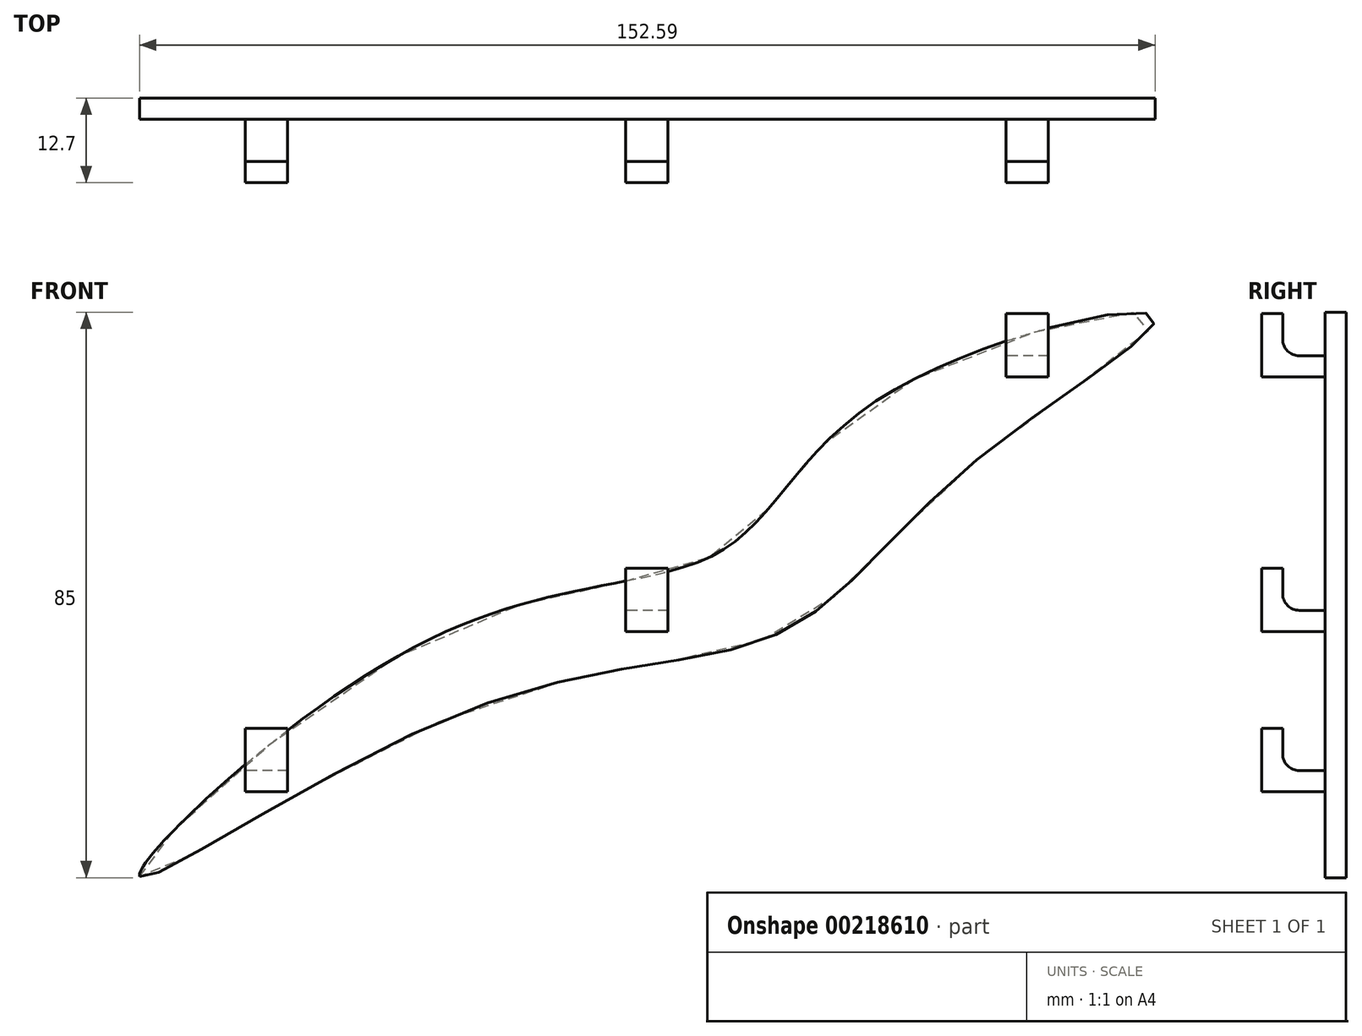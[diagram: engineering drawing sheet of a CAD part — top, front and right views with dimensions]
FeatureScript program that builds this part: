
annotation { "Feature Type Name" : "Feature", "Feature Type Description" : "" }
export const myFeature = defineFeature(function(context is Context, id is Id, definition is map)
    precondition{}
    {
        {
            var Q0;
            Q0=qCreatedBy(makeId("Front.planeOp"),FACE);
            var sketch = newSketch(context, id + "F0", { "sketchPlane" : qUnion([Q0])});
            skFitSpline(sketch, "E0", {"points": [v(0, 0) * mm, v(43.31, 35.58) * mm, v(87.55, 49.08) * mm, v(110.94, 71.7) * mm, v(152.4, 84.17) * mm, v(125.2, 62.2) * mm, v(96.47, 36.79) * mm, v(49.64, 25.18) * mm, v(0, 0) * mm]});
            skSolve(sketch);
        }
        {
            var Q0;
            Q0 = qSketchRegion(id + "F0", true);
            extrude(context, id + "F1", {"entities" : qUnion([Q0]), "depth" : 3.17 * mm});
        }
        {
            var Q0;
            Q0=qCreatedBy(makeId("Right.planeOp"),FACE);
            cPlane(context, id + "F2", {"entities" : qUnion([Q0]), "cplaneType" : CPlaneType.OFFSET, "offset" : 19.05 * mm, "width" : 152.4 * mm, "height" : 152.4 * mm});
        }
        {
            var Q0;
            Q0=qCreatedBy(id+"F2.planeOp",FACE);
            var sketch = newSketch(context, id + "F3", { "sketchPlane" : qUnion([Q0])});
            skLineSegment(sketch, "E1", {"start": v(-3.17, 12.76) * mm, "end": v(-12.7, 12.76) * mm});
            skLineSegment(sketch, "E2", {"start": v(-12.7, 12.76) * mm, "end": v(-12.7, 22.28) * mm});
            skLineSegment(sketch, "E3", {"start": v(-12.7, 22.28) * mm, "end": v(-9.52, 22.28) * mm});
            skLineSegment(sketch, "E4", {"start": v(-9.52, 22.28) * mm, "end": v(-9.52, 15.93) * mm});
            skLineSegment(sketch, "E5", {"start": v(-9.52, 15.93) * mm, "end": v(-3.18, 15.93) * mm});
            skLineSegment(sketch, "E6", {"start": v(-3.18, 15.93) * mm, "end": v(-3.18, 12.76) * mm});
            skSolve(sketch);
        }
        {
            var Q0;
            Q0 = qSketchRegion(id + "F3", true);
            extrude(context, id + "F4", {"entities" : qUnion([Q0]), "operationType" : NewBodyOperationType.ADD, "depth" : 6.35 * mm, "symmetric" : true});
        }
        {
            var Q0;
            Q0=qCreatedBy(makeId("Right.planeOp"),FACE);
            cPlane(context, id + "F5", {"entities" : qUnion([Q0]), "cplaneType" : CPlaneType.OFFSET, "offset" : 76.2 * mm, "width" : 152.4 * mm, "height" : 152.4 * mm});
        }
        {
            var Q0;
            Q0=qCreatedBy(id+"F5.planeOp",FACE);
            var sketch = newSketch(context, id + "F6", { "sketchPlane" : qUnion([Q0])});
            skLineSegment(sketch, "E7", {"start": v(-3.18, 36.86) * mm, "end": v(-12.7, 36.86) * mm});
            skLineSegment(sketch, "E8", {"start": v(-12.7, 36.86) * mm, "end": v(-12.7, 46.38) * mm});
            skLineSegment(sketch, "E9", {"start": v(-12.7, 46.38) * mm, "end": v(-9.53, 46.38) * mm});
            skLineSegment(sketch, "E10", {"start": v(-9.53, 46.38) * mm, "end": v(-9.53, 40.03) * mm});
            skLineSegment(sketch, "E11", {"start": v(-9.53, 40.03) * mm, "end": v(-3.18, 40.03) * mm});
            skLineSegment(sketch, "E12", {"start": v(-3.18, 40.03) * mm, "end": v(-3.18, 36.86) * mm});
            skSolve(sketch);
        }
        {
            var Q0;
            Q0 = qSketchRegion(id + "F6", true);
            extrude(context, id + "F7", {"entities" : qUnion([Q0]), "operationType" : NewBodyOperationType.ADD, "depth" : 6.35 * mm, "symmetric" : true});
        }
        {
            var Q0;
            Q0=qCreatedBy(makeId("Right.planeOp"),FACE);
            cPlane(context, id + "F8", {"entities" : qUnion([Q0]), "cplaneType" : CPlaneType.OFFSET, "offset" : 133.35 * mm, "width" : 152.4 * mm, "height" : 152.4 * mm});
        }
        {
            var Q0;
            Q0=qCreatedBy(id+"F8.planeOp",FACE);
            var sketch = newSketch(context, id + "F9", { "sketchPlane" : qUnion([Q0])});
            skLineSegment(sketch, "E13", {"start": v(-3.18, 75.11) * mm, "end": v(-12.7, 75.11) * mm});
            skLineSegment(sketch, "E14", {"start": v(-12.7, 75.11) * mm, "end": v(-12.7, 84.64) * mm});
            skLineSegment(sketch, "E15", {"start": v(-12.7, 84.64) * mm, "end": v(-9.53, 84.64) * mm});
            skLineSegment(sketch, "E16", {"start": v(-9.53, 84.64) * mm, "end": v(-9.53, 78.29) * mm});
            skLineSegment(sketch, "E17", {"start": v(-9.53, 78.29) * mm, "end": v(-3.17, 78.29) * mm});
            skLineSegment(sketch, "E18", {"start": v(-3.17, 78.29) * mm, "end": v(-3.17, 75.11) * mm});
            skSolve(sketch);
        }
        {
            var Q0;
            Q0 = qSketchRegion(id + "F9", true);
            extrude(context, id + "F10", {"entities" : qUnion([Q0]), "operationType" : NewBodyOperationType.ADD, "depth" : 6.35 * mm, "symmetric" : true});
        }
        {
            var Q0;
            Q0=makeQuery(id+"F4.opExtrude","SWEPT_EDGE",EDGE,{"disambiguationData":[OSD([sQuery(id+"F3.wireOp",EDGE,"E1"),sQuery(id+"F3.wireOp",EDGE,"E6")])]});
            var Q1;
            Q1=makeQuery(id+"F4.opExtrude","CAP_EDGE",EDGE,{"disambiguationData":[OSD([sQuery(id+"F3.wireOp",EDGE,"E6")])],"isStart":false});
            var Q2;
            Q2=makeQuery(id+"F4.opExtrude","CAP_EDGE",EDGE,{"disambiguationData":[OSD([sQuery(id+"F3.wireOp",EDGE,"E6")])],"isStart":true});
            var Q3;
            Q3=makeQuery(id+"F4.opExtrude","SWEPT_EDGE",EDGE,{"disambiguationData":[OSD([sQuery(id+"F3.wireOp",EDGE,"E5"),sQuery(id+"F3.wireOp",EDGE,"E6")])]});
            var Q4;
            Q4=makeQuery(id+"F4.opExtrude","SWEPT_EDGE",EDGE,{"disambiguationData":[OSD([sQuery(id+"F3.wireOp",EDGE,"E4"),sQuery(id+"F3.wireOp",EDGE,"E5")])]});
            var Q5;
            Q5=makeQuery(id+"F7.opExtrude","SWEPT_EDGE",EDGE,{"disambiguationData":[OSD([sQuery(id+"F6.wireOp",EDGE,"E11"),sQuery(id+"F6.wireOp",EDGE,"E12")])]});
            var Q6;
            Q6=makeQuery(id+"F7.opExtrude","CAP_EDGE",EDGE,{"disambiguationData":[OSD([sQuery(id+"F6.wireOp",EDGE,"E12")])],"isStart":true});
            var Q7;
            Q7=makeQuery(id+"F7.opExtrude","SWEPT_EDGE",EDGE,{"disambiguationData":[OSD([sQuery(id+"F6.wireOp",EDGE,"E7"),sQuery(id+"F6.wireOp",EDGE,"E12")])]});
            var Q8;
            Q8=makeQuery(id+"F7.opExtrude","CAP_EDGE",EDGE,{"disambiguationData":[OSD([sQuery(id+"F6.wireOp",EDGE,"E12")])],"isStart":false});
            var Q9;
            Q9=makeQuery(id+"F7.opExtrude","SWEPT_EDGE",EDGE,{"disambiguationData":[OSD([sQuery(id+"F6.wireOp",EDGE,"E10"),sQuery(id+"F6.wireOp",EDGE,"E11")])]});
            var Q10;
            Q10=makeQuery(id+"F10.opExtrude","CAP_EDGE",EDGE,{"disambiguationData":[OSD([sQuery(id+"F9.wireOp",EDGE,"E18")])],"isStart":false});
            var Q11;
            Q11=makeQuery(id+"F10.opExtrude","SWEPT_EDGE",EDGE,{"disambiguationData":[OSD([sQuery(id+"F9.wireOp",EDGE,"E17"),sQuery(id+"F9.wireOp",EDGE,"E18")])]});
            var Q12;
            Q12=makeQuery(id+"F10.opExtrude","SWEPT_EDGE",EDGE,{"disambiguationData":[OSD([sQuery(id+"F9.wireOp",EDGE,"E16"),sQuery(id+"F9.wireOp",EDGE,"E17")])]});
            var Q13;
            Q13=makeQuery(id+"F10.opExtrude","SWEPT_EDGE",EDGE,{"disambiguationData":[OSD([sQuery(id+"F9.wireOp",EDGE,"E13"),sQuery(id+"F9.wireOp",EDGE,"E18")])]});
            var Q14;
            Q14=makeQuery(id+"F10.opExtrude","CAP_EDGE",EDGE,{"disambiguationData":[OSD([sQuery(id+"F9.wireOp",EDGE,"E18")])],"isStart":true});
            fillet(context, id + "F11", {"entities" : qUnion([Q0, Q1, Q2, Q3, Q4, Q5, Q6, Q7, Q8, Q9, Q10, Q11, Q12, Q13, Q14]), "radius" : 2.54 * mm, "tangentPropagation" : true, "allowEdgeOverflow" : false});
        }
    });
